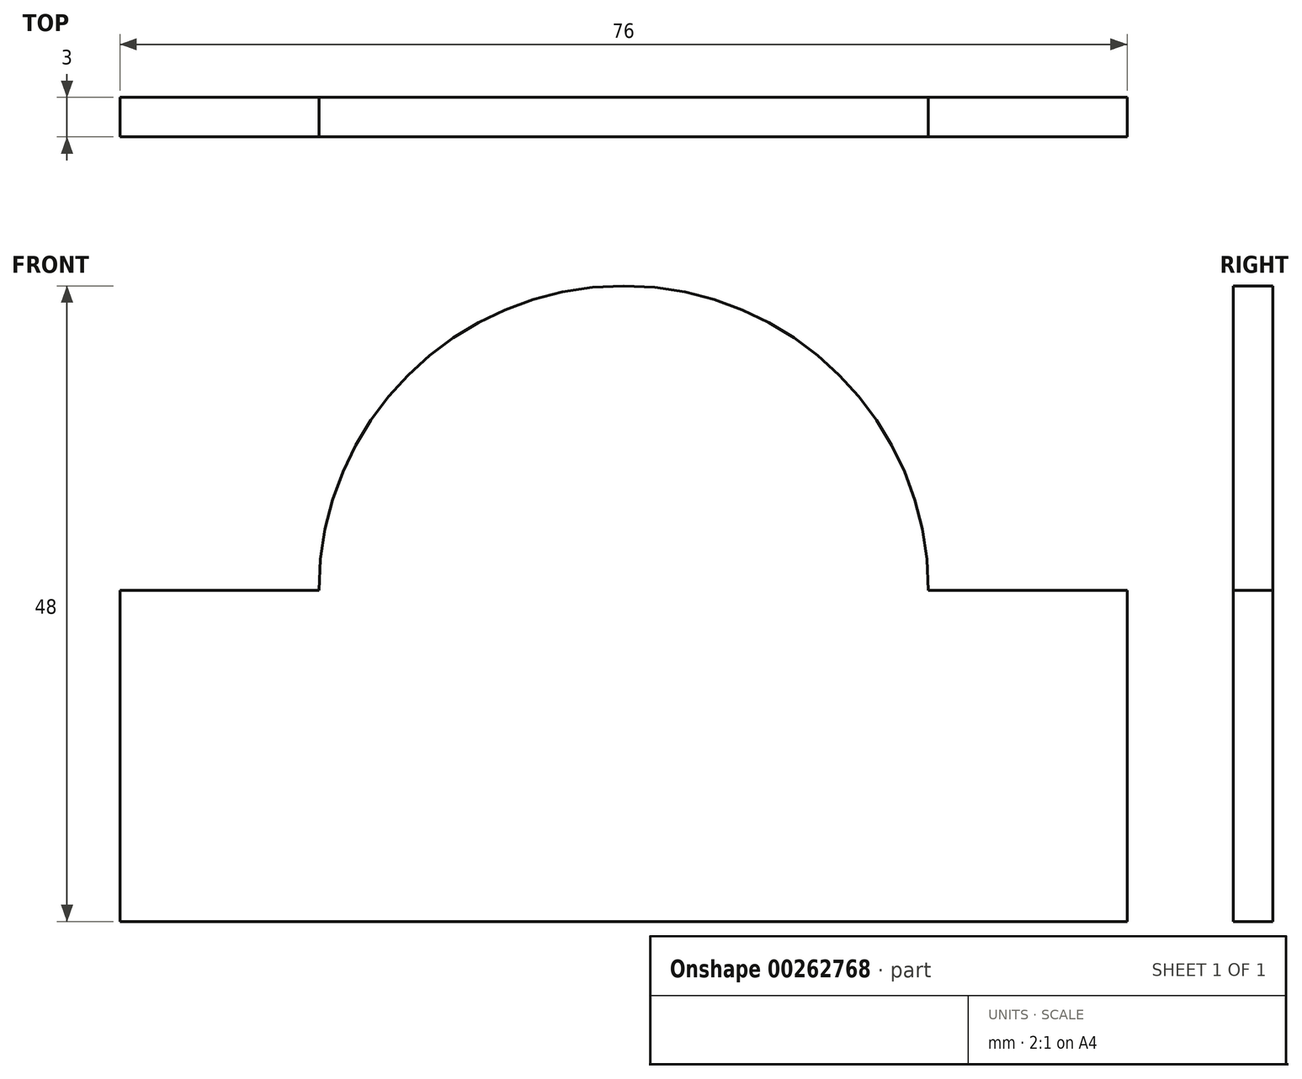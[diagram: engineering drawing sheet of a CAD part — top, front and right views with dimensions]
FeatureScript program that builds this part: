
annotation { "Feature Type Name" : "Feature", "Feature Type Description" : "" }
export const myFeature = defineFeature(function(context is Context, id is Id, definition is map)
    precondition{}
    {
        {
            var Q0;
            Q0=qCreatedBy(makeId("Front.planeOp"),FACE);
            var sketch = newSketch(context, id + "F0", { "sketchPlane" : qUnion([Q0])});
            skLineSegment(sketch, "E0.bottom", {"start": v(-39.44, 45.85) * mm, "end": v(-24.44, 45.85) * mm});
            skLineSegment(sketch, "E0.top", {"start": v(-39.44, 20.85) * mm, "end": v(36.56, 20.85) * mm});
            skLineSegment(sketch, "E0.left", {"start": v(-39.44, 45.85) * mm, "end": v(-39.44, 20.85) * mm});
            skLineSegment(sketch, "E0.right", {"start": v(36.56, 45.85) * mm, "end": v(36.56, 20.85) * mm});
            skPoint(sketch, "E1", {"position": v(-1.44, 45.85) * mm});
            skArc(sketch, "E2", {"start": v(21.56, 45.85) * mm, "mid": v(-1.44, 68.85) * mm, "end": v(-24.44, 45.85) * mm});
            skLineSegment(sketch, "E3.trimOffspring", {"start": v(21.56, 45.85) * mm, "end": v(36.56, 45.85) * mm});
            skSolve(sketch);
        }
        {
            var Q0;
            Q0=makeQuery(id+"F0.imprint","IMPRINT",FACE,{"disambiguationData":[TD([[makeQuery(id+"F0.imprint","IMPRINT",EDGE,{"derivedFrom":sQuery(id+"F0.wireOp",EDGE,"E0.bottom")}),-1.0]])]});
            extrude(context, id + "F1", {"entities" : qUnion([Q0]), "depth" : 3 * mm});
        }
    });
